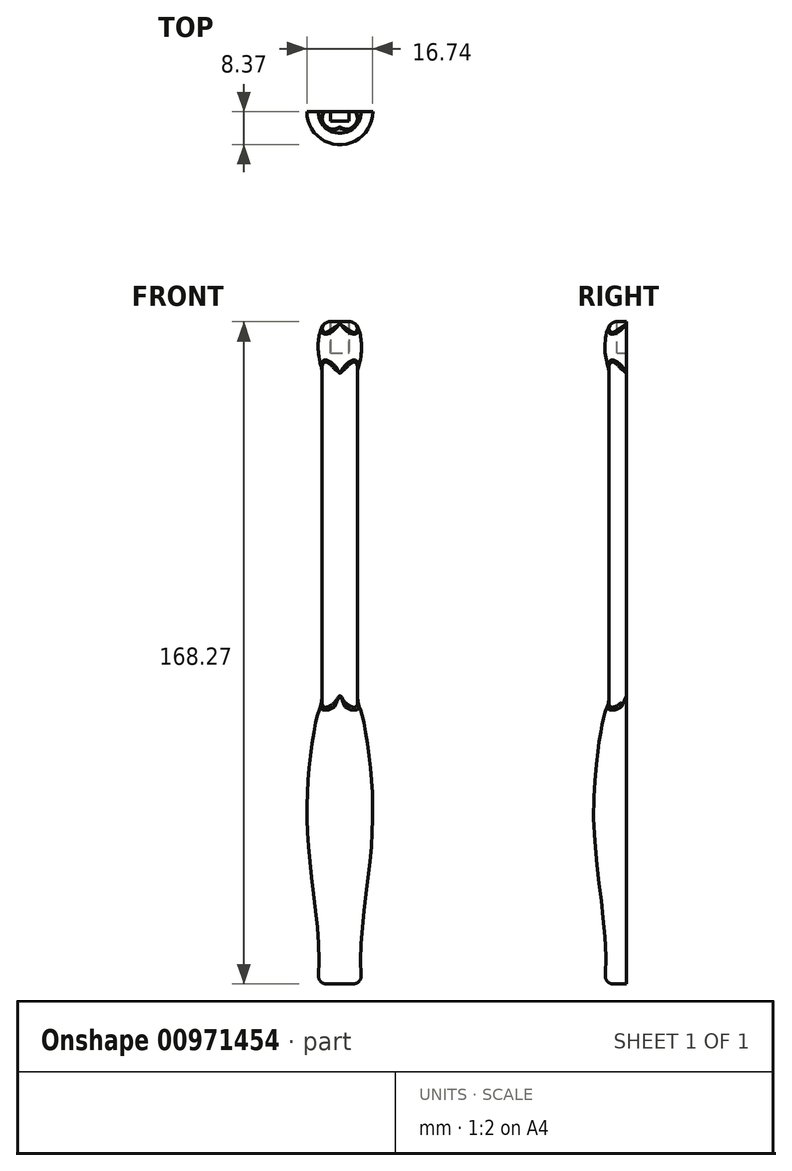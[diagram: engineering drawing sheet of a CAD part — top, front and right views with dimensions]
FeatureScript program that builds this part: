
annotation { "Feature Type Name" : "Feature", "Feature Type Description" : "" }
export const myFeature = defineFeature(function(context is Context, id is Id, definition is map)
    precondition{}
    {
        {
            var Q0;
            Q0=qCreatedBy(makeId("Top.planeOp"),FACE);
            var sketch = newSketch(context, id + "F0", { "sketchPlane" : qUnion([Q0])});
            skCircle(sketch, "E0", {"center": v(0, 0) * mm, "radius": 4.5 * mm, "construction": true});
            skLineSegment(sketch, "E1.bottom", {"start": v(-1.5, -4.5) * mm, "end": v(1.5, -4.5) * mm});
            skLineSegment(sketch, "E1.top", {"start": v(-1.5, 4.5) * mm, "end": v(1.5, 4.5) * mm});
            skLineSegment(sketch, "E1.left", {"start": v(-4.5, -1.5) * mm, "end": v(-4.5, 1.5) * mm});
            skLineSegment(sketch, "E1.right", {"start": v(4.5, -1.5) * mm, "end": v(4.5, 1.5) * mm});
            skPoint(sketch, "E2.visualSharp", {"position": v(4.5, -4.5) * mm});
            skArc(sketch, "E2.filletArc", {"start": v(1.5, -4.5) * mm, "mid": v(3.62, -3.62) * mm, "end": v(4.5, -1.5) * mm});
            skPoint(sketch, "E3.visualSharp", {"position": v(-4.5, -4.5) * mm});
            skArc(sketch, "E3.filletArc", {"start": v(-4.5, -1.5) * mm, "mid": v(-3.62, -3.62) * mm, "end": v(-1.5, -4.5) * mm});
            skPoint(sketch, "E4.visualSharp", {"position": v(-4.5, 4.5) * mm});
            skArc(sketch, "E4.filletArc", {"start": v(-1.5, 4.5) * mm, "mid": v(-3.62, 3.62) * mm, "end": v(-4.5, 1.5) * mm});
            skPoint(sketch, "E5.visualSharp", {"position": v(4.5, 4.5) * mm});
            skArc(sketch, "E5.filletArc", {"start": v(4.5, 1.5) * mm, "mid": v(3.62, 3.62) * mm, "end": v(1.5, 4.5) * mm});
            skSolve(sketch);
        }
        {
            var Q0;
            Q0 = qSketchRegion(id + "F0", true);
            extrude(context, id + "F1", {"entities" : qUnion([Q0]), "depth" : 100 * mm, "offsetDistance" : 25 * mm});
        }
        {
            var Q0;
            Q0=makeQuery(id+"F1.opExtrude","CAP_FACE",FACE,{"disambiguationData":[OSD([sQuery(id+"F0.wireOp",EDGE,"E1.bottom"),sQuery(id+"F0.wireOp",EDGE,"E1.top"),sQuery(id+"F0.wireOp",EDGE,"E1.left"),sQuery(id+"F0.wireOp",EDGE,"E1.right"),sQuery(id+"F0.wireOp",EDGE,"E2.filletArc"),sQuery(id+"F0.wireOp",EDGE,"E3.filletArc"),sQuery(id+"F0.wireOp",EDGE,"E4.filletArc"),sQuery(id+"F0.wireOp",EDGE,"E5.filletArc")])],"isStart":false});
            var sketch = newSketch(context, id + "F2", { "sketchPlane" : qUnion([Q0])});
            skLineSegment(sketch, "E6.bottom", {"start": v(-2.35, -2.45) * mm, "end": v(2.35, -2.45) * mm});
            skLineSegment(sketch, "E6.top", {"start": v(-2.35, 2.45) * mm, "end": v(2.35, 2.45) * mm});
            skLineSegment(sketch, "E6.left", {"start": v(-2.35, -2.45) * mm, "end": v(-2.35, 2.45) * mm});
            skLineSegment(sketch, "E6.right", {"start": v(2.35, -2.45) * mm, "end": v(2.35, 2.45) * mm});
            skPoint(sketch, "E6.middle", {"position": v(0, 0) * mm});
            skSolve(sketch);
        }
        {
            var Q0;
            Q0=makeQuery(id+"F2.imprint","IMPRINT",FACE,{"disambiguationData":[TD([[makeQuery(id+"F2.imprint","IMPRINT",EDGE,{"derivedFrom":sQuery(id+"F2.wireOp",EDGE,"E6.bottom")}),1.0]])]});
            extrude(context, id + "F3", {"entities" : qUnion([Q0]), "operationType" : NewBodyOperationType.REMOVE, "oppositeDirection" : true, "depth" : 8 * mm, "offsetDistance" : 25 * mm});
        }
        {
            var Q0;
            Q0=qCreatedBy(makeId("Front.planeOp"),FACE);
            var sketch = newSketch(context, id + "F4", { "sketchPlane" : qUnion([Q0])});
            skLineSegment(sketch, "E7.bottom", {"start": v(-45.7, 121.47) * mm, "end": v(79.52, 121.47) * mm});
            skLineSegment(sketch, "E7.top", {"start": v(-45.7, -130.48) * mm, "end": v(79.52, -130.48) * mm});
            skLineSegment(sketch, "E7.left", {"start": v(-45.7, 121.47) * mm, "end": v(-45.7, -130.48) * mm});
            skLineSegment(sketch, "E7.right", {"start": v(79.52, 121.47) * mm, "end": v(79.52, -130.48) * mm});
            skSolve(sketch);
        }
        {
            var Q0;
            Q0=qCreatedBy(makeId("Front.planeOp"),FACE);
            var sketch = newSketch(context, id + "F5", { "sketchPlane" : qUnion([Q0])});
            skFitSpline(sketch, "E8", {"points": [v(-4.5, 7.2) * mm, v(-4.69, 2.86) * mm, v(-5.4, 0.92) * mm, v(-7.67, -12.35) * mm, v(-7.88, -34.7) * mm, v(-5.6, -68.27) * mm], "startDerivative": vector(0.74, -31.54) * mm, "endDerivative": vector(-10.87, -92.17) * mm});
            skLineSegment(sketch, "E9", {"start": v(-4.5, 7.2) * mm, "end": v(0, 7.2) * mm});
            skLineSegment(sketch, "E10", {"start": v(0, 7.2) * mm, "end": v(0, -68.27) * mm});
            skLineSegment(sketch, "E11", {"start": v(0, -68.27) * mm, "end": v(-5.6, -68.27) * mm});
            skSolve(sketch);
        }
        {
            var Q0;
            Q0=makeQuery(id+"F5.imprint","IMPRINT",FACE,{"disambiguationData":[TD([[makeQuery(id+"F5.imprint","IMPRINT",EDGE,{"derivedFrom":sQuery(id+"F5.wireOp",EDGE,"E8")}),1.0]])]});
            var Q1;
            Q1=sQuery(id+"F5.wireOp",EDGE,"E10");
            revolve(context, id + "F6", {"operationType" : NewBodyOperationType.ADD, "surfaceOperationType" : NewSurfaceOperationType.NEW, "entities" : qUnion([Q0]), "axis" : qUnion([Q1]), "revolveType" : RevolveType.FULL});
        }
        {
            var Q0;
            Q0=makeQuery(id+"F1.opExtrude","CAP_EDGE",EDGE,{"disambiguationData":[OSD([sQuery(id+"F0.wireOp",EDGE,"E1.right")])],"isStart":false});
            var Q1;
            Q1=makeQuery(id+"F6.boolean.opBoolean","INTERSECT",EDGE,{"derivedFrom":[makeQuery(id+"F1.opExtrude","SWEPT_FACE",FACE,{"disambiguationData":[OSD([sQuery(id+"F0.wireOp",EDGE,"E3.filletArc")])]}),makeQuery(id+"F6.opRevolve","SWEPT_FACE",FACE,{"disambiguationData":[OSD([sQuery(id+"F5.wireOp",EDGE,"E8")])]})]});
            var Q2;
            Q2=makeQuery(id+"F6.boolean.opBoolean","INTERSECT",EDGE,{"derivedFrom":[makeQuery(id+"F1.opExtrude","SWEPT_FACE",FACE,{"disambiguationData":[OSD([sQuery(id+"F0.wireOp",EDGE,"E1.bottom")])]}),makeQuery(id+"F6.opRevolve","SWEPT_FACE",FACE,{"disambiguationData":[OSD([sQuery(id+"F5.wireOp",EDGE,"E8")])]})]});
            var Q3;
            Q3=makeQuery(id+"F6.opRevolve","SWEPT_EDGE",EDGE,{"disambiguationData":[OSD([sQuery(id+"F5.wireOp",EDGE,"E8"),sQuery(id+"F5.wireOp",EDGE,"E11")])]});
            fillet(context, id + "F7", {"entities" : qUnion([Q0, Q1, Q2, Q3]), "radius" : 2 * mm, "tangentPropagation" : true, "allowEdgeOverflow" : false});
        }
        {
            var Q0;
            Q0=qCreatedBy(makeId("Front.planeOp"),FACE);
            var sketch = newSketch(context, id + "F8", { "sketchPlane" : qUnion([Q0])});
            skLineSegment(sketch, "E12.0", {"start": v(-2.5, 92) * mm, "end": v(2.5, 92) * mm, "construction": true});
            skFitSpline(sketch, "E13", {"points": [v(-3.84, 99.49) * mm, v(-5.01, 97.4) * mm, v(-5.35, 95.86) * mm, v(-5.49, 94.42) * mm, v(-5.49, 92.96) * mm, v(-5.3, 90.87) * mm, v(-4.7, 88.45) * mm, v(-4.56, 87.79) * mm, v(-4.5, 86.82) * mm], "startDerivative": vector(-11.5, -10.37) * mm, "endDerivative": vector(-0.02, -10.52) * mm});
            skLineSegment(sketch, "E14", {"start": v(-3.84, 99.49) * mm, "end": v(-3.84, 86.16) * mm});
            skLineSegment(sketch, "E15", {"start": v(-3.84, 86.16) * mm, "end": v(-4.5, 86.82) * mm});
            skSolve(sketch);
        }
        {
            var Q0;
            Q0=makeQuery(id+"F8.imprint","IMPRINT",FACE,{"disambiguationData":[TD([[makeQuery(id+"F8.imprint","IMPRINT",EDGE,{"derivedFrom":sQuery(id+"F8.wireOp",EDGE,"E13")}),1.0]])]});
            var Q1;
            Q1=makeQuery(id+"F6.opRevolve","SWEPT_FACE",FACE,{"disambiguationData":[OSD([sQuery(id+"F5.wireOp",EDGE,"E8")])]});
            revolve(context, id + "F9", {"operationType" : NewBodyOperationType.ADD, "surfaceOperationType" : NewSurfaceOperationType.NEW, "entities" : qUnion([Q0]), "axis" : qUnion([Q1]), "revolveType" : RevolveType.FULL});
        }
        {
            var Q0;
            Q0 = qSketchRegion(id + "F4", true);
            extrude(context, id + "F10", {"entities" : qUnion([Q0]), "operationType" : NewBodyOperationType.REMOVE, "oppositeDirection" : true, "depth" : 25 * mm, "offsetDistance" : 25 * mm});
        }
        {
            var Q0;
            Q0=makeQuery(id+"F9.boolean.opBoolean","INTERSECT",EDGE,{"disambiguationData":[OD(1.0)],"derivedFrom":[makeQuery(id+"F1.opExtrude","SWEPT_FACE",FACE,{"disambiguationData":[OSD([sQuery(id+"F0.wireOp",EDGE,"E2.filletArc")])]}),makeQuery(id+"F9.opRevolve","SWEPT_FACE",FACE,{"disambiguationData":[OSD([sQuery(id+"F8.wireOp",EDGE,"E13")])]})]});
            var Q1;
            Q1=makeQuery(id+"F9.boolean.opBoolean","INTERSECT",EDGE,{"disambiguationData":[OD(1.0)],"derivedFrom":[makeQuery(id+"F7.opFillet","BLEND_FACE",FACE,{"disambiguationData":[OSD([sQuery(id+"F0.wireOp",EDGE,"E1.bottom")])]}),makeQuery(id+"F9.opRevolve","SWEPT_FACE",FACE,{"disambiguationData":[OSD([sQuery(id+"F8.wireOp",EDGE,"E13")])]})]});
            var Q2;
            Q2=makeQuery(id+"F9.boolean.opBoolean","INTERSECT",EDGE,{"disambiguationData":[OD(0.0)],"derivedFrom":[makeQuery(id+"F1.opExtrude","SWEPT_FACE",FACE,{"disambiguationData":[OSD([sQuery(id+"F0.wireOp",EDGE,"E2.filletArc")])]}),makeQuery(id+"F9.opRevolve","SWEPT_FACE",FACE,{"disambiguationData":[OSD([sQuery(id+"F8.wireOp",EDGE,"E13")])]})]});
            var Q3;
            Q3=makeQuery(id+"F9.boolean.opBoolean","INTERSECT",EDGE,{"disambiguationData":[OD(0.0)],"derivedFrom":[makeQuery(id+"F1.opExtrude","SWEPT_FACE",FACE,{"disambiguationData":[OSD([sQuery(id+"F0.wireOp",EDGE,"E3.filletArc")])]}),makeQuery(id+"F9.opRevolve","SWEPT_FACE",FACE,{"disambiguationData":[OSD([sQuery(id+"F8.wireOp",EDGE,"E13")])]})]});
            var Q4;
            Q4=makeQuery(id+"F9.boolean.opBoolean","INTERSECT",EDGE,{"disambiguationData":[OD(0.0)],"derivedFrom":[makeQuery(id+"F1.opExtrude","SWEPT_FACE",FACE,{"disambiguationData":[OSD([sQuery(id+"F0.wireOp",EDGE,"E1.bottom")])]}),makeQuery(id+"F9.opRevolve","SWEPT_FACE",FACE,{"disambiguationData":[OSD([sQuery(id+"F8.wireOp",EDGE,"E13")])]})]});
            var Q5;
            Q5=makeQuery(id+"F9.boolean.opBoolean","INTERSECT",EDGE,{"disambiguationData":[OD(1.0)],"derivedFrom":[makeQuery(id+"F1.opExtrude","SWEPT_FACE",FACE,{"disambiguationData":[OSD([sQuery(id+"F0.wireOp",EDGE,"E1.bottom")])]}),makeQuery(id+"F9.opRevolve","SWEPT_FACE",FACE,{"disambiguationData":[OSD([sQuery(id+"F8.wireOp",EDGE,"E13")])]})]});
            var Q6;
            Q6=makeQuery(id+"F9.boolean.opBoolean","INTERSECT",EDGE,{"disambiguationData":[OD(0.0)],"derivedFrom":[makeQuery(id+"F1.opExtrude","SWEPT_FACE",FACE,{"disambiguationData":[OSD([sQuery(id+"F0.wireOp",EDGE,"E1.right")])]}),makeQuery(id+"F9.opRevolve","SWEPT_FACE",FACE,{"disambiguationData":[OSD([sQuery(id+"F8.wireOp",EDGE,"E13")])]})]});
            var Q7;
            Q7=makeQuery(id+"F9.boolean.opBoolean","INTERSECT",EDGE,{"disambiguationData":[OD(0.0)],"derivedFrom":[makeQuery(id+"F7.opFillet","BLEND_FACE",FACE,{"disambiguationData":[OSD([sQuery(id+"F0.wireOp",EDGE,"E1.bottom")])]}),makeQuery(id+"F9.opRevolve","SWEPT_FACE",FACE,{"disambiguationData":[OSD([sQuery(id+"F8.wireOp",EDGE,"E13")])]})]});
            var Q8;
            Q8=makeQuery(id+"F9.boolean.opBoolean","INTERSECT",EDGE,{"disambiguationData":[OD(1.0)],"derivedFrom":[makeQuery(id+"F1.opExtrude","SWEPT_FACE",FACE,{"disambiguationData":[OSD([sQuery(id+"F0.wireOp",EDGE,"E3.filletArc")])]}),makeQuery(id+"F9.opRevolve","SWEPT_FACE",FACE,{"disambiguationData":[OSD([sQuery(id+"F8.wireOp",EDGE,"E13")])]})]});
            var Q9;
            Q9=makeQuery(id+"F9.boolean.opBoolean","INTERSECT",EDGE,{"disambiguationData":[OD(0.0)],"derivedFrom":[makeQuery(id+"F7.opFillet","BLEND_FACE",FACE,{"disambiguationData":[OSD([sQuery(id+"F0.wireOp",EDGE,"E3.filletArc")])]}),makeQuery(id+"F9.opRevolve","SWEPT_FACE",FACE,{"disambiguationData":[OSD([sQuery(id+"F8.wireOp",EDGE,"E13")])]})]});
            var Q10;
            Q10=makeQuery(id+"F9.boolean.opBoolean","INTERSECT",EDGE,{"disambiguationData":[OD(0.0)],"derivedFrom":[makeQuery(id+"F7.opFillet","BLEND_FACE",FACE,{"disambiguationData":[OSD([sQuery(id+"F0.wireOp",EDGE,"E2.filletArc")])]}),makeQuery(id+"F9.opRevolve","SWEPT_FACE",FACE,{"disambiguationData":[OSD([sQuery(id+"F8.wireOp",EDGE,"E13")])]})]});
            var Q11;
            Q11=makeQuery(id+"F9.boolean.opBoolean","INTERSECT",EDGE,{"disambiguationData":[OD(0.0)],"derivedFrom":[makeQuery(id+"F7.opFillet","BLEND_FACE",FACE,{"disambiguationData":[OSD([sQuery(id+"F0.wireOp",EDGE,"E1.right")])]}),makeQuery(id+"F9.opRevolve","SWEPT_FACE",FACE,{"disambiguationData":[OSD([sQuery(id+"F8.wireOp",EDGE,"E13")])]})]});
            var Q12;
            Q12=makeQuery(id+"F9.boolean.opBoolean","INTERSECT",EDGE,{"disambiguationData":[OD(1.0)],"derivedFrom":[makeQuery(id+"F7.opFillet","BLEND_FACE",FACE,{"disambiguationData":[OSD([sQuery(id+"F0.wireOp",EDGE,"E2.filletArc")])]}),makeQuery(id+"F9.opRevolve","SWEPT_FACE",FACE,{"disambiguationData":[OSD([sQuery(id+"F8.wireOp",EDGE,"E13")])]})]});
            var Q13;
            Q13=makeQuery(id+"F9.boolean.opBoolean","INTERSECT",EDGE,{"disambiguationData":[OD(1.0)],"derivedFrom":[makeQuery(id+"F7.opFillet","BLEND_FACE",FACE,{"disambiguationData":[OSD([sQuery(id+"F0.wireOp",EDGE,"E3.filletArc")])]}),makeQuery(id+"F9.opRevolve","SWEPT_FACE",FACE,{"disambiguationData":[OSD([sQuery(id+"F8.wireOp",EDGE,"E13")])]})]});
            var Q14;
            Q14=makeQuery(id+"F9.boolean.opBoolean","INTERSECT",EDGE,{"disambiguationData":[OD(0.0)],"derivedFrom":[makeQuery(id+"F7.opFillet","BLEND_FACE",FACE,{"disambiguationData":[OSD([sQuery(id+"F0.wireOp",EDGE,"E1.left")])]}),makeQuery(id+"F9.opRevolve","SWEPT_FACE",FACE,{"disambiguationData":[OSD([sQuery(id+"F8.wireOp",EDGE,"E13")])]})]});
            fillet(context, id + "F11", {"entities" : qUnion([Q0, Q1, Q2, Q3, Q4, Q5, Q6, Q7, Q8, Q9, Q10, Q11, Q12, Q13, Q14]), "radius" : 2 * mm, "tangentPropagation" : true, "allowEdgeOverflow" : false});
        }
    });
